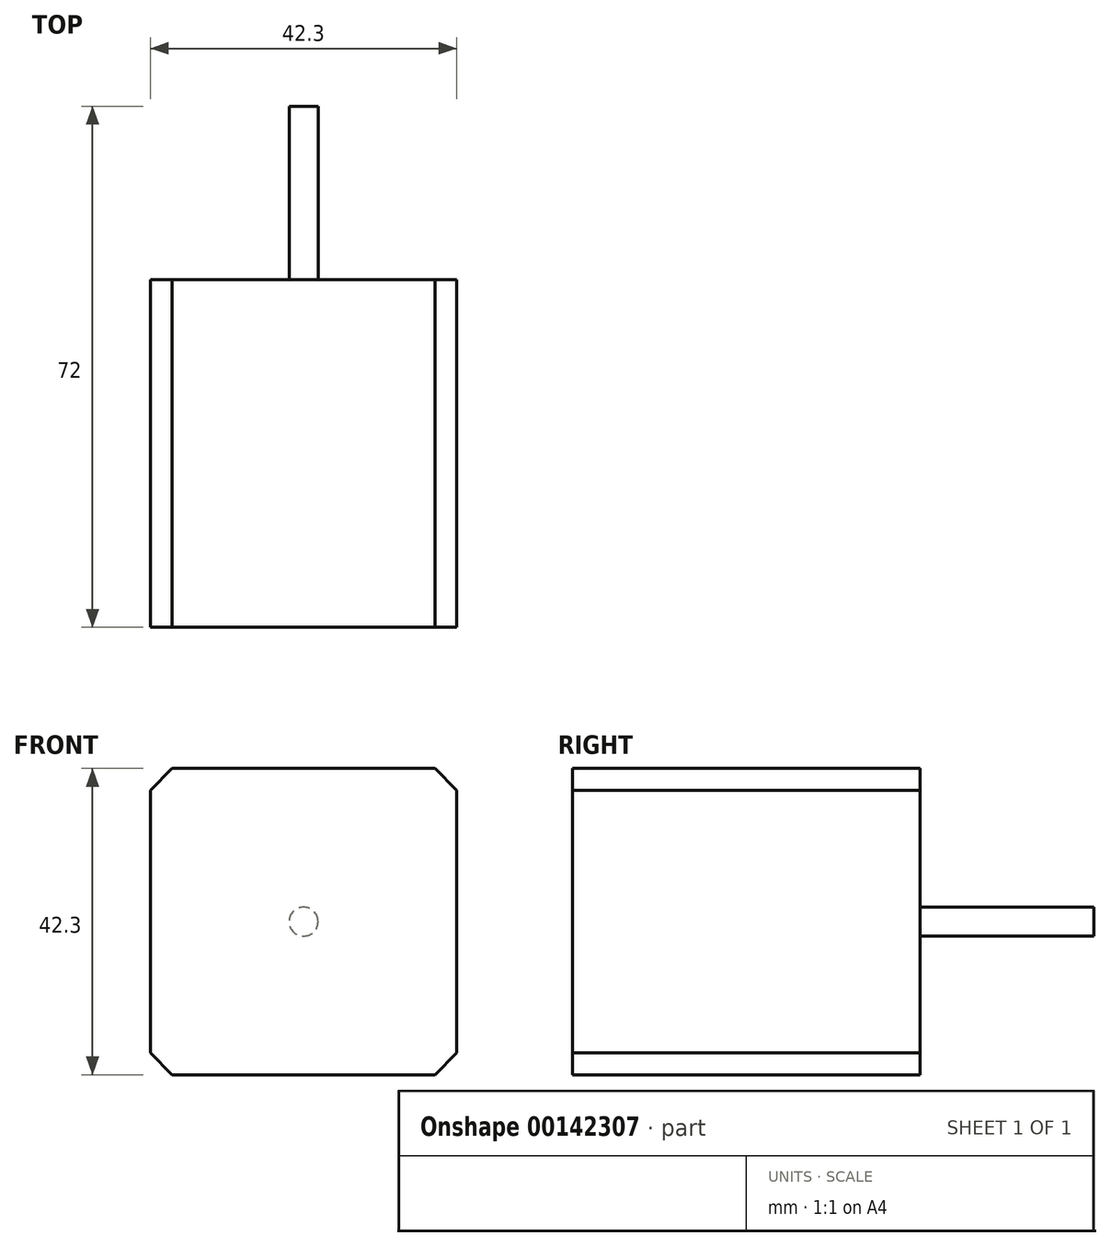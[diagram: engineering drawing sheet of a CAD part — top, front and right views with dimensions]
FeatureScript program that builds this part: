
annotation { "Feature Type Name" : "Feature", "Feature Type Description" : "" }
export const myFeature = defineFeature(function(context is Context, id is Id, definition is map)
    precondition{}
    {
        {
            var Q0;
            Q0=qCreatedBy(makeId("Front.planeOp"),FACE);
            var sketch = newSketch(context, id + "F0", { "sketchPlane" : qUnion([Q0])});
            skLineSegment(sketch, "E0.bottom", {"start": v(21.15, 21.15) * mm, "end": v(-21.15, 21.15) * mm});
            skLineSegment(sketch, "E0.top", {"start": v(21.15, -21.15) * mm, "end": v(-21.15, -21.15) * mm});
            skLineSegment(sketch, "E0.left", {"start": v(21.15, 21.15) * mm, "end": v(21.15, -21.15) * mm});
            skLineSegment(sketch, "E0.right", {"start": v(-21.15, 21.15) * mm, "end": v(-21.15, -21.15) * mm});
            skPoint(sketch, "E0.middle", {"position": v(0, 0) * mm});
            skCircle(sketch, "E1", {"center": v(0, 0) * mm, "radius": 2 * mm});
            skSolve(sketch);
        }
        {
            var Q0;
            Q0=makeQuery(id+"F0.imprint","IMPRINT",FACE,{"disambiguationData":[TD([[makeQuery(id+"F0.imprint","IMPRINT",EDGE,{"derivedFrom":sQuery(id+"F0.wireOp",EDGE,"E0.bottom")}),1.0]])]});
            var Q1;
            Q1=makeQuery(id+"F0.imprint","IMPRINT",FACE,{"disambiguationData":[TD([[makeQuery(id+"F0.imprint","IMPRINT",EDGE,{"derivedFrom":sQuery(id+"F0.wireOp",EDGE,"E1")}),1.0]])]});
            extrude(context, id + "F1", {"entities" : qUnion([Q0, Q1]), "depth" : 48 * mm});
        }
        {
            var Q0;
            Q0=makeQuery(id+"F0.imprint","IMPRINT",FACE,{"disambiguationData":[TD([[makeQuery(id+"F0.imprint","IMPRINT",EDGE,{"derivedFrom":sQuery(id+"F0.wireOp",EDGE,"E1")}),1.0]])]});
            extrude(context, id + "F2", {"entities" : qUnion([Q0]), "operationType" : NewBodyOperationType.ADD, "oppositeDirection" : true, "depth" : 24 * mm});
        }
        {
            var Q0;
            Q0=makeQuery(id+"F1.opExtrude","SWEPT_EDGE",EDGE,{"disambiguationData":[OSD([sQuery(id+"F0.wireOp",EDGE,"E0.bottom"),sQuery(id+"F0.wireOp",EDGE,"E0.left")])]});
            var Q1;
            Q1=makeQuery(id+"F1.opExtrude","SWEPT_EDGE",EDGE,{"disambiguationData":[OSD([sQuery(id+"F0.wireOp",EDGE,"E0.bottom"),sQuery(id+"F0.wireOp",EDGE,"E0.right")])]});
            var Q2;
            Q2=makeQuery(id+"F1.opExtrude","SWEPT_EDGE",EDGE,{"disambiguationData":[OSD([sQuery(id+"F0.wireOp",EDGE,"E0.top"),sQuery(id+"F0.wireOp",EDGE,"E0.left")])]});
            var Q3;
            Q3=makeQuery(id+"F1.opExtrude","SWEPT_EDGE",EDGE,{"disambiguationData":[OSD([sQuery(id+"F0.wireOp",EDGE,"E0.top"),sQuery(id+"F0.wireOp",EDGE,"E0.right")])]});
            chamfer(context, id + "F3", {"entities" : qUnion([Q0, Q1, Q2, Q3]), "width" : 3 * mm, "tangentPropagation" : true});
        }
    });
